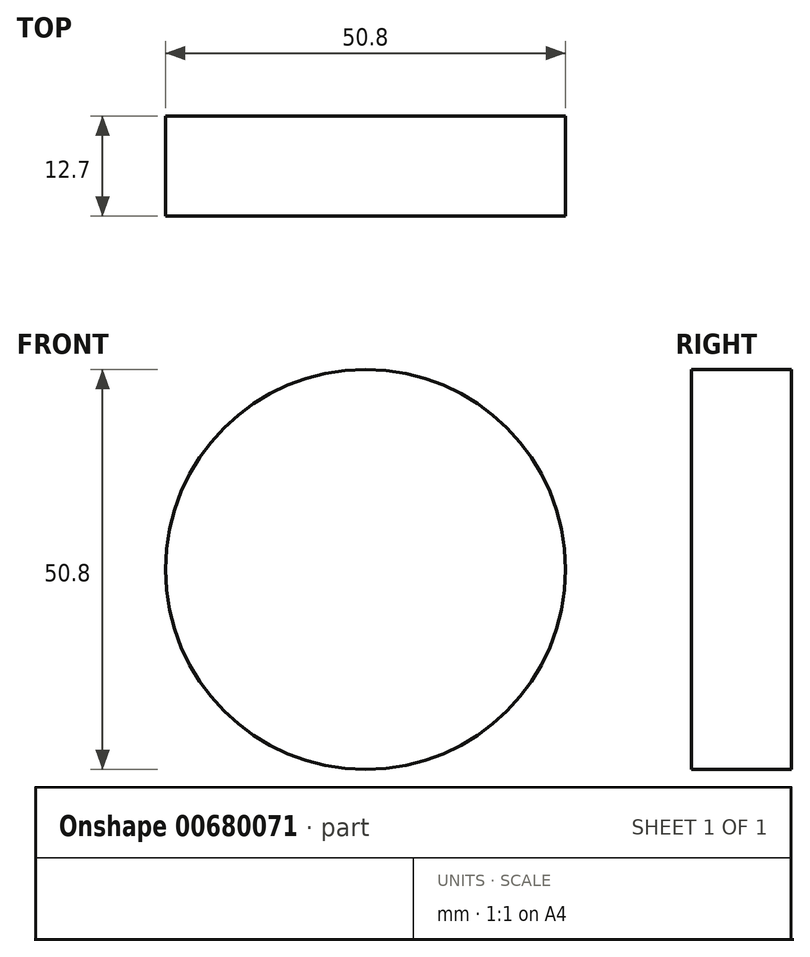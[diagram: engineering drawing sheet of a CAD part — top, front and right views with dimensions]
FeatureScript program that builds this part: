
annotation { "Feature Type Name" : "Feature", "Feature Type Description" : "" }
export const myFeature = defineFeature(function(context is Context, id is Id, definition is map)
    precondition{}
    {
        {
            var Q0;
            Q0=qCreatedBy(makeId("Front.planeOp"),FACE);
            var sketch = newSketch(context, id + "F0", { "sketchPlane" : qUnion([Q0])});
            skCircle(sketch, "E0", {"center": v(0, 0) * mm, "radius": 25.4 * mm});
            skSolve(sketch);
        }
        {
            var Q0;
            Q0=makeQuery(id+"F0.imprint","IMPRINT",FACE,{"disambiguationData":[TD([[makeQuery(id+"F0.imprint","IMPRINT",EDGE,{"derivedFrom":sQuery(id+"F0.wireOp",EDGE,"E0")}),1.0]])]});
            extrude(context, id + "F1", {"entities" : qUnion([Q0]), "depth" : 12.7 * mm, "offsetDistance" : 25.4 * mm});
        }
    });
